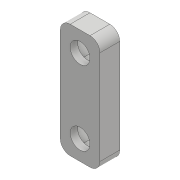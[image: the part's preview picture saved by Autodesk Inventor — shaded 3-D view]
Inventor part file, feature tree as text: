
AUTODESK INVENTOR PART (.ipt)
format: ipt  version: 2017 (Build 210142000, 142)  size: 127,488 bytes
history: native  units: mm
features: sketch x3, extrude x2, projected_geometry x2, fillet x1, hole x1
ambient origin geometry x8: Origin, YZ Plane, XZ Plane, XY Plane, X Axis, Y Axis, Z Axis, Center Point
bodies: Solid1 (feature_tree)
feature tree (9):
  extrude  "Extrusion1"  Depth=23.0mm
  extrude  "Extrusion2"  TaperAngle=0.0deg  [1 undecoded]
  fillet  "Fillet1"  Radius=7.5mm
  hole  "Hole1"  [1 undecoded]
  sketch  "Sketch1"  dims[d0=8.0mm d1=23.0mm]
  sketch  "Sketch2"  dims[d2=4.0mm d3=0.0mm d4=0.0mm d5=7.5mm]
  sketch  "Sketch3"  dims[d6=5.5mm d7=2.5mm d8=0.0mm d9=2.0mm d10=4.0mm d11=6.0mm d12=4.0mm d13=2.0mm d14=90.0deg d15=8.0mm d16=20.594885mm d17=2.75mm d18=2.75mm]
  projected_geometry  "Projected Loop1"
  projected_geometry  "Projected Loop2"
note: 2 required parameter values undecoded (feature->parameter linkage not recoverable at this tier; creation-order binding heuristic only, values carry confidence <= 0.55)
